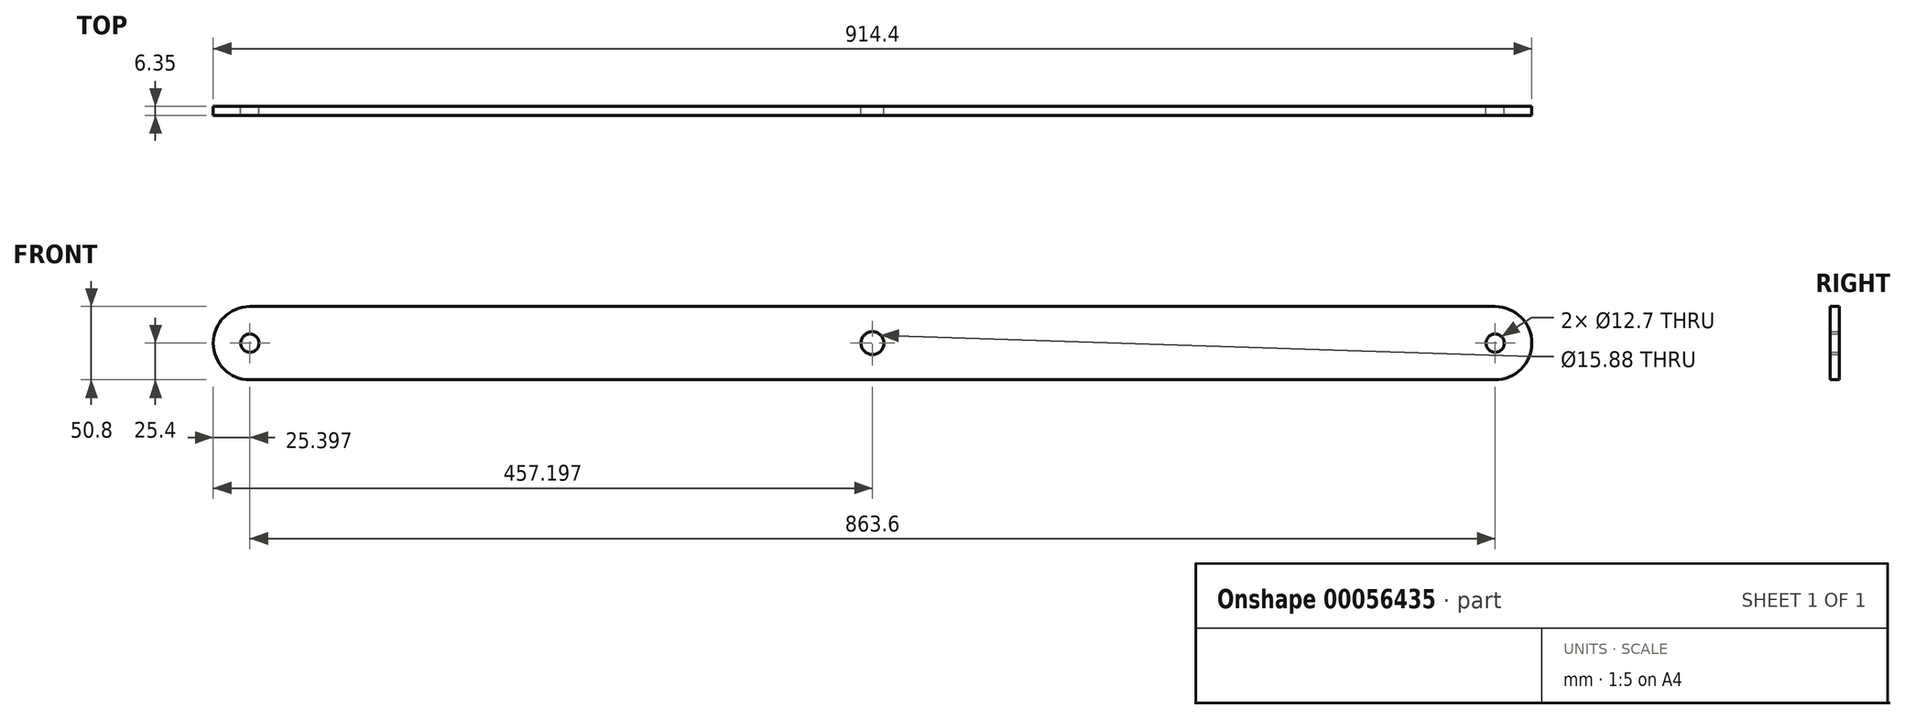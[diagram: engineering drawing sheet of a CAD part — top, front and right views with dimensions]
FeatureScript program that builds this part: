
annotation { "Feature Type Name" : "Feature", "Feature Type Description" : "" }
export const myFeature = defineFeature(function(context is Context, id is Id, definition is map)
    precondition{}
    {
        {
            var Q0;
            Q0=qCreatedBy(makeId("Front.planeOp"),FACE);
            var sketch = newSketch(context, id + "F0", { "sketchPlane" : qUnion([Q0])});
            skLineSegment(sketch, "E0.bottom", {"start": v(-556.94, 50.8) * mm, "end": v(306.66, 50.8) * mm});
            skLineSegment(sketch, "E0.top", {"start": v(-556.94, 0) * mm, "end": v(306.66, 0) * mm});
            skLineSegment(sketch, "E0.left", {"start": v(-556.94, 50.8) * mm, "end": v(-556.94, 0) * mm});
            skLineSegment(sketch, "E0.right", {"start": v(306.66, 50.8) * mm, "end": v(306.66, 0) * mm});
            skCircle(sketch, "E1", {"center": v(-556.94, 25.4) * mm, "radius": 25.4 * mm});
            skCircle(sketch, "E2", {"center": v(306.66, 25.4) * mm, "radius": 25.4 * mm});
            skCircle(sketch, "E3", {"center": v(-125.14, 25.4) * mm, "radius": 25.4 * mm});
            skPoint(sketch, "E3.centerSnap0", {"position": v(-125.14, 50.8) * mm});
            skCircle(sketch, "E4", {"center": v(-556.94, 25.4) * mm, "radius": 6.35 * mm});
            skCircle(sketch, "E5", {"center": v(-125.14, 25.4) * mm, "radius": 7.94 * mm});
            skCircle(sketch, "E6", {"center": v(306.66, 25.4) * mm, "radius": 6.35 * mm});
            skSolve(sketch);
        }
        {
            var Q0;
            {var subQ2=sQuery(id+"F0.wireOp",EDGE,"E0.bottom");var subQ4=sQuery(id+"F0.wireOp",EDGE,"E3");var subQ5=makeQuery(id+"F0.imprint","INTERSECT",VERTEX,{"derivedFrom":[subQ2,subQ4]});Q0=makeQuery(id+"F0.imprint","IMPRINT",FACE,{"disambiguationData":[TD([[makeQuery(id+"F0.imprint","IMPRINT",EDGE,{"disambiguationData":[TD([[subQ5,1.0]])],"derivedFrom":subQ4}),-1.0]])]});}
            var Q1;
            {var subQ1=sQuery(id+"F0.wireOp",EDGE,"E0.left");var subQ3=sQuery(id+"F0.wireOp",EDGE,"E4");var subQ4=makeQuery(id+"F0.imprint","INTERSECT",VERTEX,{"disambiguationData":[OD(0.0)],"derivedFrom":[subQ1,subQ3]});Q1=makeQuery(id+"F0.imprint","IMPRINT",FACE,{"disambiguationData":[TD([[makeQuery(id+"F0.imprint","IMPRINT",EDGE,{"disambiguationData":[TD([[subQ4,-1.0]])],"derivedFrom":subQ3}),-1.0]])]});}
            var Q2;
            {var subQ1=sQuery(id+"F0.wireOp",EDGE,"E0.right");var subQ3=sQuery(id+"F0.wireOp",EDGE,"E6");var subQ4=makeQuery(id+"F0.imprint","INTERSECT",VERTEX,{"disambiguationData":[OD(0.0)],"derivedFrom":[subQ1,subQ3]});Q2=makeQuery(id+"F0.imprint","IMPRINT",FACE,{"disambiguationData":[TD([[makeQuery(id+"F0.imprint","IMPRINT",EDGE,{"disambiguationData":[TD([[subQ4,1.0]])],"derivedFrom":subQ3}),-1.0]])]});}
            var Q3;
            {var subQ1=sQuery(id+"F0.wireOp",EDGE,"E0.left");var subQ3=sQuery(id+"F0.wireOp",EDGE,"E4");var subQ4=makeQuery(id+"F0.imprint","INTERSECT",VERTEX,{"disambiguationData":[OD(0.0)],"derivedFrom":[subQ1,subQ3]});Q3=makeQuery(id+"F0.imprint","IMPRINT",FACE,{"disambiguationData":[TD([[makeQuery(id+"F0.imprint","IMPRINT",EDGE,{"disambiguationData":[TD([[subQ4,1.0]])],"derivedFrom":subQ3}),-1.0]])]});}
            var Q4;
            {var subQ1=sQuery(id+"F0.wireOp",EDGE,"E0.right");var subQ3=sQuery(id+"F0.wireOp",EDGE,"E6");var subQ4=makeQuery(id+"F0.imprint","INTERSECT",VERTEX,{"disambiguationData":[OD(0.0)],"derivedFrom":[subQ1,subQ3]});Q4=makeQuery(id+"F0.imprint","IMPRINT",FACE,{"disambiguationData":[TD([[makeQuery(id+"F0.imprint","IMPRINT",EDGE,{"disambiguationData":[TD([[subQ4,-1.0]])],"derivedFrom":subQ3}),-1.0]])]});}
            var Q5;
            Q5=makeQuery(id+"F0.imprint","IMPRINT",FACE,{"disambiguationData":[TD([[makeQuery(id+"F0.imprint","IMPRINT",EDGE,{"derivedFrom":sQuery(id+"F0.wireOp",EDGE,"E5")}),-1.0]])]});
            var Q6;
            {var subQ2=sQuery(id+"F0.wireOp",EDGE,"E0.bottom");var subQ4=sQuery(id+"F0.wireOp",EDGE,"E3");var subQ5=makeQuery(id+"F0.imprint","INTERSECT",VERTEX,{"derivedFrom":[subQ2,subQ4]});Q6=makeQuery(id+"F0.imprint","IMPRINT",FACE,{"disambiguationData":[TD([[makeQuery(id+"F0.imprint","IMPRINT",EDGE,{"disambiguationData":[TD([[subQ5,-1.0]])],"derivedFrom":subQ4}),-1.0]])]});}
            extrude(context, id + "F1", {"entities" : qUnion([Q0, Q1, Q2, Q3, Q4, Q5, Q6]), "depth" : 6.35 * mm});
        }
    });
